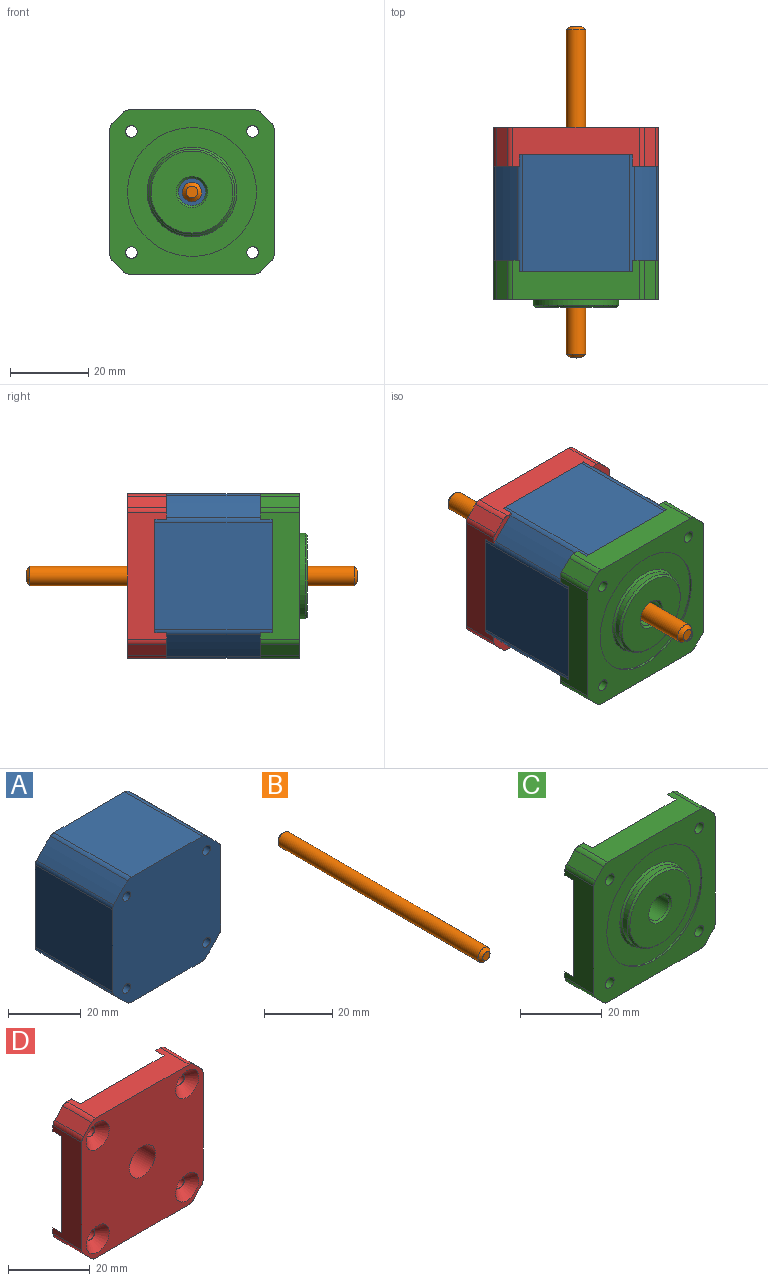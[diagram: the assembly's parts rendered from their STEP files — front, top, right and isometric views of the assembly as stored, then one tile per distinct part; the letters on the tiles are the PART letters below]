
ASSEMBLY  parts=4 mates=3
PART A: 22 faces, bbox 42x30x42 mm
  f0: cylinder r=55mm len=30mm, axis (0,1,0), area 230.4mm2, adj f8,f9,f10,f17
  f1: plane 30x27.54mm, normal (1,0,0), area 826.2mm2, adj f8,f9,f10,f11
  f2: cylinder r=55mm len=30mm, axis (0,1,0), area 230.4mm2, adj f8,f9,f11,f12
  f3: plane 30x27.54mm, normal (0,0,1), area 826.2mm2, adj f8,f9,f12,f13
  f4: cylinder r=55mm len=30mm, axis (0,1,0), area 230.4mm2, adj f8,f9,f13,f14
  f5: plane 30x27.54mm, normal (-1,0,0), area 826.2mm2, adj f8,f9,f14,f15
  f6: cylinder r=55mm len=30mm, axis (0,1,0), area 230.4mm2, adj f8,f9,f15,f16
  f7: plane 30x27.54mm, normal (0,0,-1), area 826.2mm2, adj f8,f9,f16,f17
  f8: plane 42x42mm, normal (0,-1,0), area 1655.7mm2, adj f0,f1,f2,f3,f4,f5,f6,f7
  f9: plane 42x42mm, normal (0,1,0), area 1655.7mm2, adj f0,f1,f2,f3,f4,f5,f6,f7
  f10: cylinder r=2mm len=30mm, axis (0,1,0), area 42.9mm2, adj f0,f1,f8,f9
  f11: cylinder r=2mm len=30mm, axis (0,1,0), area 42.9mm2, adj f1,f2,f8,f9
  f12: cylinder r=2mm len=30mm, axis (0,1,0), area 42.9mm2, adj f2,f3,f8,f9
  f13: cylinder r=2mm len=30mm, axis (0,1,0), area 42.9mm2, adj f3,f4,f8,f9
  f14: cylinder r=2mm len=30mm, axis (0,1,0), area 42.9mm2, adj f4,f5,f8,f9
  f15: cylinder r=2mm len=30mm, axis (0,1,0), area 42.9mm2, adj f5,f6,f8,f9
  f16: cylinder r=2mm len=30mm, axis (0,1,0), area 42.9mm2, adj f6,f7,f8,f9
  f17: cylinder r=2mm len=30mm, axis (0,1,0), area 42.9mm2, adj f0,f7,f8,f9
  f18: cylinder r=1.5mm len=30mm, axis (0,-1,0), area 282.7mm2, adj f8,f9
  f19: cylinder r=1.5mm len=30mm, axis (0,-1,0), area 282.7mm2, adj f8,f9
  f20: cylinder r=1.5mm len=30mm, axis (0,-1,0), area 282.7mm2, adj f8,f9
  f21: cylinder r=1.5mm len=30mm, axis (0,-1,0), area 282.7mm2, adj f8,f9
PART B: 5 faces, bbox 5x85x5 mm
  f0: cylinder r=2.5mm len=83mm, axis (0,1,0), area 1303.8mm2, adj f3,f4
  f1: plane 3x3mm, normal (0,-1,0), area 7.1mm2, adj f4
  f2: plane 3x3mm, normal (0,1,0), area 7.1mm2, adj f3
  f3: cone r=2.5mm half-angle=45deg, axis (0,-1,0), area 17.8mm2, adj f0,f2
  f4: cone r=1.5mm half-angle=45deg, axis (0,1,0), area 17.8mm2, adj f0,f1
PART C: 38 faces, bbox 42x12x42 mm
  f0: plane 32.34x10mm, normal (1,0,0), area 236.4mm2, adj f3,f4,f9,f20,f21,f29,f31,f32
  f1: plane 32.34x10mm, normal (0,0,1), area 236.4mm2, adj f2,f3,f9,f18,f19,f29,f30,f31
  f2: plane 6.49x6.49mm, normal (0,1,0), area 11.7mm2, adj f1,f7,f13,f19,f23,f30
  f3: plane 6.49x6.49mm, normal (0,1,0), area 11.7mm2, adj f0,f1,f12,f18,f21,f31
  f4: plane 6.49x6.49mm, normal (0,1,0), area 11.7mm2, adj f0,f8,f11,f20,f25,f32
  f5: plane 6.49x6.49mm, normal (0,1,0), area 11.7mm2, adj f7,f8,f10,f22,f24,f33
  f6: cylinder r=3.5mm len=8.5mm, axis (0,-1,0), area 186.9mm2, adj f27,f29
  f7: plane 32.34x10mm, normal (-1,0,0), area 236.4mm2, adj f2,f5,f9,f22,f23,f29,f30,f33
  f8: plane 32.34x10mm, normal (0,0,-1), area 236.4mm2, adj f4,f5,f9,f24,f25,f29,f32,f33
  f9: plane 42x42mm, normal (0,-1,0), area 847.7mm2, adj f0,f1,f7,f8,f10,f11,f12,f13
  f10: plane 10x2.83mm, normal (-0.71,0,-0.71), area 40mm2, adj f5,f9,f22,f24
  f11: plane 10x2.83mm, normal (0.71,0,-0.71), area 40mm2, adj f4,f9,f20,f25
  f12: plane 10x2.83mm, normal (0.71,0,0.71), area 40mm2, adj f3,f9,f18,f21
  f13: plane 10x2.83mm, normal (-0.71,0,0.71), area 40mm2, adj f2,f9,f19,f23
  f14: cylinder r=16.5mm len=33mm, axis (0,-1,0), area 51.8mm2, adj f9,f15
  f15: plane 33x33mm, normal (0,-1,0), area 439.8mm2, adj f14,f26
  f16: cylinder r=11mm len=22mm, axis (0,1,0), area 103.7mm2, adj f26,f28
  f17: plane 21x21mm, normal (0,-1,0), area 296.1mm2, adj f27,f28
  f18: cylinder r=2mm len=10mm, axis (0,-1,0), area 15.7mm2, adj f1,f3,f9,f12
  f19: cylinder r=2mm len=10mm, axis (0,-1,0), area 15.7mm2, adj f1,f2,f9,f13
  f20: cylinder r=2mm len=10mm, axis (0,1,0), area 15.7mm2, adj f0,f4,f9,f11
  f21: cylinder r=2mm len=10mm, axis (0,1,0), area 15.7mm2, adj f0,f3,f9,f12
  f22: cylinder r=2mm len=10mm, axis (0,-1,0), area 15.7mm2, adj f5,f7,f9,f10
  f23: cylinder r=2mm len=10mm, axis (0,-1,0), area 15.7mm2, adj f2,f7,f9,f13
  f24: cylinder r=2mm len=10mm, axis (0,1,0), area 15.7mm2, adj f5,f8,f9,f10
  f25: cylinder r=2mm len=10mm, axis (0,1,0), area 15.7mm2, adj f4,f8,f9,f11
  f26: cone r=11mm half-angle=45deg, axis (0,1,0), area 50mm2, adj f15,f16
  f27: cone r=3.5mm half-angle=45deg, axis (0,-1,0), area 16.7mm2, adj f6,f17
  f28: cone r=10.5mm half-angle=45deg, axis (0,1,0), area 47.8mm2, adj f16,f17
  f29: plane 42x42mm, normal (0,1,0), area 1617.7mm2, adj f0,f1,f6,f7,f8,f30,f31,f32
  f30: cylinder r=55mm len=6.49mm, axis (0,1,0), area 27.6mm2, adj f1,f2,f7,f29
  f31: cylinder r=55mm len=6.49mm, axis (0,1,0), area 27.6mm2, adj f0,f1,f3,f29
  f32: cylinder r=55mm len=6.49mm, axis (0,1,0), area 27.6mm2, adj f0,f4,f8,f29
  f33: cylinder r=55mm len=6.49mm, axis (0,1,0), area 27.6mm2, adj f5,f7,f8,f29
  f34: cylinder r=1.5mm len=7mm, axis (0,-1,0), area 66mm2, adj f9,f29
  f35: cylinder r=1.5mm len=7mm, axis (0,-1,0), area 66mm2, adj f9,f29
  f36: cylinder r=1.5mm len=7mm, axis (0,-1,0), area 66mm2, adj f9,f29
  f37: cylinder r=1.5mm len=7mm, axis (0,-1,0), area 66mm2, adj f9,f29
PART D: 35 faces, bbox 42x10x42 mm
  f0: plane 32.34x10mm, normal (1,0,0), area 236.4mm2, adj f3,f4,f8,f15,f16,f22,f23,f25
  f1: plane 32.34x10mm, normal (0,0,1), area 236.4mm2, adj f2,f3,f8,f13,f14,f21,f22,f25
  f2: plane 6.49x6.49mm, normal (0,1,0), area 11.7mm2, adj f1,f6,f12,f14,f18,f21
  f3: plane 6.49x6.49mm, normal (0,1,0), area 11.7mm2, adj f0,f1,f11,f13,f16,f22
  f4: plane 6.49x6.49mm, normal (0,1,0), area 11.7mm2, adj f0,f7,f10,f15,f20,f23
  f5: plane 6.49x6.49mm, normal (0,1,0), area 11.7mm2, adj f6,f7,f9,f17,f19,f24
  f6: plane 32.34x10mm, normal (-1,0,0), area 236.4mm2, adj f2,f5,f8,f17,f18,f21,f24,f25
  f7: plane 32.34x10mm, normal (0,0,-1), area 236.4mm2, adj f4,f5,f8,f19,f20,f23,f24,f25
  f8: plane 42x42mm, normal (0,-1,0), area 1466.6mm2, adj f0,f1,f6,f7,f9,f10,f11,f12
  f9: plane 10x2.83mm, normal (-0.71,0,-0.71), area 40mm2, adj f5,f8,f17,f19
  f10: plane 10x2.83mm, normal (0.71,0,-0.71), area 40mm2, adj f4,f8,f15,f20
  f11: plane 10x2.83mm, normal (0.71,0,0.71), area 40mm2, adj f3,f8,f13,f16
  f12: plane 10x2.83mm, normal (-0.71,0,0.71), area 40mm2, adj f2,f8,f14,f18
  f13: cylinder r=2mm len=10mm, axis (0,-1,0), area 15.7mm2, adj f1,f3,f8,f11
  f14: cylinder r=2mm len=10mm, axis (0,-1,0), area 15.7mm2, adj f1,f2,f8,f12
  f15: cylinder r=2mm len=10mm, axis (0,1,0), area 15.7mm2, adj f0,f4,f8,f10
  f16: cylinder r=2mm len=10mm, axis (0,1,0), area 15.7mm2, adj f0,f3,f8,f11
  f17: cylinder r=2mm len=10mm, axis (0,-1,0), area 15.7mm2, adj f5,f6,f8,f9
  f18: cylinder r=2mm len=10mm, axis (0,-1,0), area 15.7mm2, adj f2,f6,f8,f12
  f19: cylinder r=2mm len=10mm, axis (0,1,0), area 15.7mm2, adj f5,f7,f8,f9
  f20: cylinder r=2mm len=10mm, axis (0,1,0), area 15.7mm2, adj f4,f7,f8,f10
  f21: cylinder r=55mm len=6.49mm, axis (0,1,0), area 27.6mm2, adj f1,f2,f6,f25
  f22: cylinder r=55mm len=6.49mm, axis (0,1,0), area 27.6mm2, adj f0,f1,f3,f25
  f23: cylinder r=55mm len=6.49mm, axis (0,1,0), area 27.6mm2, adj f0,f4,f7,f25
  f24: cylinder r=55mm len=6.49mm, axis (0,1,0), area 27.6mm2, adj f5,f6,f7,f25
  f25: plane 42x42mm, normal (0,1,0), area 1592.6mm2, adj f0,f1,f6,f7,f21,f22,f23,f24
  f26: cylinder r=1.5mm len=4.5mm, axis (0,-1,0), area 42.4mm2, adj f25,f34
  f27: cylinder r=1.5mm len=4.5mm, axis (0,-1,0), area 42.4mm2, adj f25,f33
  f28: cylinder r=1.5mm len=4.5mm, axis (0,-1,0), area 42.4mm2, adj f25,f32
  f29: cylinder r=1.5mm len=4.5mm, axis (0,-1,0), area 42.4mm2, adj f25,f31
  f30: cylinder r=4.5mm len=9mm, axis (0,-1,0), area 197.9mm2, adj f8,f25
  f31: cone r=1.5mm half-angle=45deg, axis (0,-1,0), area 61.1mm2, adj f8,f29
  f32: cone r=1.5mm half-angle=45deg, axis (0,-1,0), area 61.1mm2, adj f8,f28
  f33: cone r=1.5mm half-angle=45deg, axis (0,-1,0), area 61.1mm2, adj f8,f27
  f34: cone r=1.5mm half-angle=45deg, axis (0,-1,0), area 61.1mm2, adj f8,f26
PLACE A t=(1.6,19.94,1.53)mm
PLACE B t=(1.6,25.44,1.53)mm
PLACE C t=(1.6,7.94,1.53)mm fixed
PLACE D rot(axis=(0,0,1),180deg) t=(1.6,31.94,1.53)mm
MATE fastened A.f19 <-> C.f34  axis (0,-1,0) through (-13.9,4.94,17.03)mm
MATE revolute B.f0 <-> C.f6  axis (0,-1,0) through (1.6,-17.06,1.53)mm
MATE fastened D.f29 <-> A.f19  axis (0,-1,0) through (-13.9,34.94,17.03)mm
